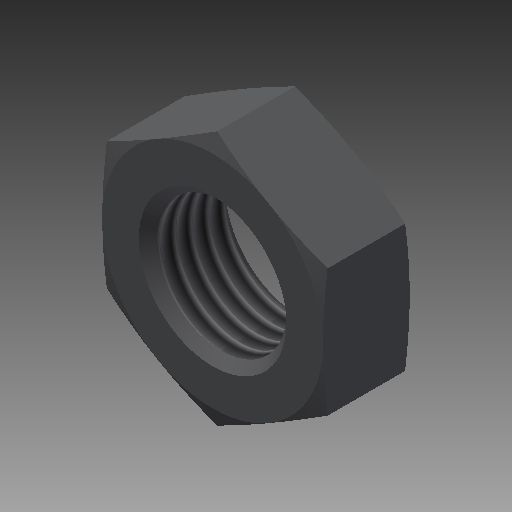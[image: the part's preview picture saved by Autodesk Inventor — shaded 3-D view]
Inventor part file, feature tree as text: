
AUTODESK INVENTOR PART (.ipt)
format: ipt  version: 2017 (Build 210142000, 142)  size: 178,688 bytes
history: native  units: in
note: dims shown in document units (in); Inventor stores cm internally (conversion verified against a paired STEP export)
features: other x70, sketch x3, revolve x2, extrude x1, thread x1
ambient origin geometry x8: Origin, YZ Plane, XZ Plane, XY Plane, X Axis, Y Axis, Z Axis, Center Point
bodies: Solid1 (feature_tree)
feature tree (77):
  sketch  "Sketch_8"  dims[d0=360.0deg d1=0.22in d2=0.0in]
  sketch  "Sketch_10"  dims[d3=360.0deg d4=0.1749in d5=0.0in]
  revolve  "Revolution1"  [1 undecoded]
  extrude  "Extrusion1"  Depth=0.1749in TaperAngle=0.0deg
  revolve  "Revolution2"  [1 undecoded]
  thread  "Thread1"  [1 undecoded]
  other  "NUT_XY"
  other  "NUT_YZ"
  other  "NUT_ZX"
  other  "NUT_X"
  other  "NUT_Y"
  other  "NUT_Z"
  other  "NUT_Center"
  other  "a1_XY"
  other  "a1_YZ"
  other  "a1_ZX"
  other  "a1_X"
  other  "a1_Y"
  other  "a1_Z"
  other  "a1_Center"
  other  "a2_XY"
  other  "a2_YZ"
  other  "a2_ZX"
  other  "a2_X"
  other  "a2_Y"
  other  "a2_Z"
  other  "a2_Center"
  other  "b1_XY"
  other  "b1_YZ"
  other  "b1_ZX"
  other  "b1_X"
  other  "b1_Y"
  other  "b1_Z"
  other  "b1_Center"
  other  "b2_XY"
  other  "b2_YZ"
  other  "b2_ZX"
  other  "b2_X"
  other  "b2_Y"
  other  "b2_Z"
  other  "b2_Center"
  other  "e_XY"
  other  "e_YZ"
  other  "e_ZX"
  other  "e_X"
  other  "e_Y"
  other  "e_Z"
  other  "e_Center"
  other  "ol1_XY"
  other  "ol1_YZ"
  other  "ol1_ZX"
  other  "ol1_X"
  other  "ol1_Y"
  other  "ol1_Z"
  other  "ol1_Center"
  other  "ol2_XY"
  other  "ol2_YZ"
  other  "ol2_ZX"
  other  "ol2_X"
  other  "ol2_Y"
  other  "ol2_Z"
  other  "ol2_Center"
  other  "th1_XY"
  other  "th1_YZ"
  other  "th1_ZX"
  other  "th1_X"
  other  "th1_Y"
  other  "th1_Z"
  other  "th1_Center"
  other  "th2_XY"
  other  "th2_YZ"
  other  "th2_ZX"
  other  "th2_X"
  other  "th2_Y"
  other  "th2_Z"
  other  "th2_Center"
  sketch  "Sketch_11"  dims[d6=0.0in]
note: 3 required parameter values undecoded (feature->parameter linkage not recoverable at this tier; creation-order binding heuristic only, values carry confidence <= 0.55)